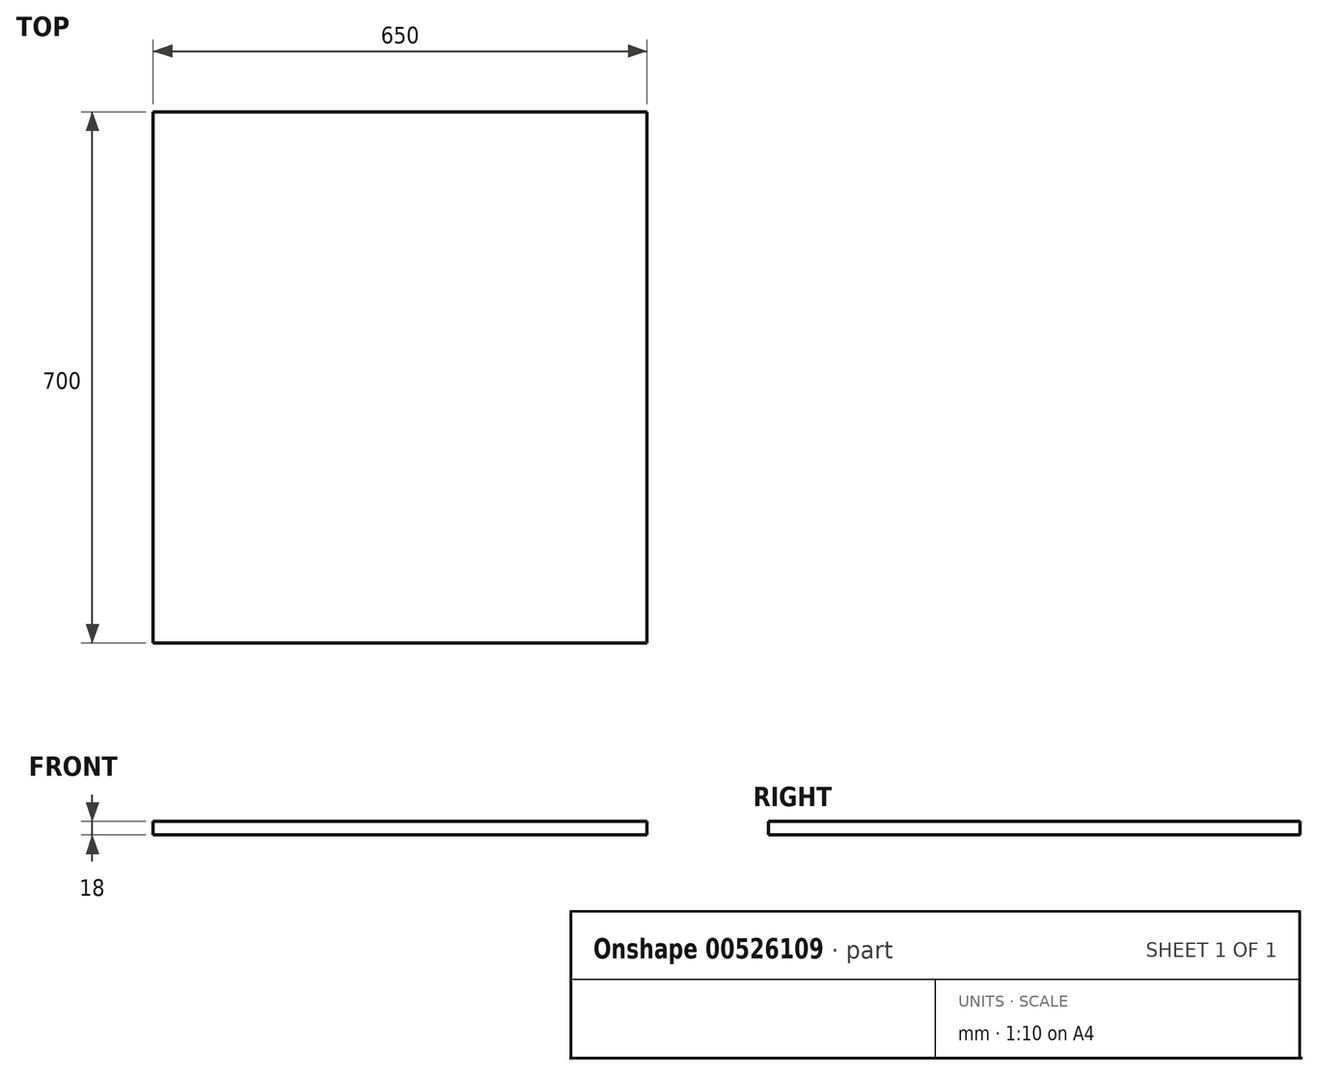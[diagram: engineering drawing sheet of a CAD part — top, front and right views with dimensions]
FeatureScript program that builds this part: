
annotation { "Feature Type Name" : "Feature", "Feature Type Description" : "" }
export const myFeature = defineFeature(function(context is Context, id is Id, definition is map)
    precondition{}
    {
        {
            var Q0;
            Q0=qCreatedBy(makeId("Top.planeOp"),FACE);
            var sketch = newSketch(context, id + "F0", { "sketchPlane" : qUnion([Q0])});
            skLineSegment(sketch, "E0.bottom", {"start": v(325, 350) * mm, "end": v(-325, 350) * mm});
            skLineSegment(sketch, "E0.top", {"start": v(325, -350) * mm, "end": v(-325, -350) * mm});
            skLineSegment(sketch, "E0.left", {"start": v(325, 350) * mm, "end": v(325, -350) * mm});
            skLineSegment(sketch, "E0.right", {"start": v(-325, 350) * mm, "end": v(-325, -350) * mm});
            skPoint(sketch, "E0.middle", {"position": v(0, 0) * mm});
            skSolve(sketch);
        }
        {
            var Q0;
            Q0=qSketchRegion(id+"F0",true);
            extrude(context, id + "F1", {"entities" : qUnion([Q0]), "depth" : 18 * mm, "offsetDistance" : 25 * mm});
        }
    });
